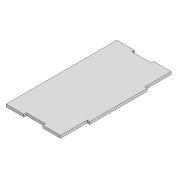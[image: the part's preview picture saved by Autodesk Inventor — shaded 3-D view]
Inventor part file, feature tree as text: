
AUTODESK INVENTOR PART (.ipt)
format: ipt  version: 2021 (Build 250183000, 183)  size: 117,760 bytes
history: native  units: mm
features: other x1, extrude x1, sketch x1
ambient origin geometry x8: Origin, YZ Plane, XZ Plane, XY Plane, X Axis, Y Axis, Z Axis, Center Point
bodies: Body1 (feature_tree)
feature tree (3):
  other  "Твердое тело1"
  extrude  "Выдавливание1"  Depth=4.0mm TaperAngle=0.0deg
  sketch  "Эскиз1"
